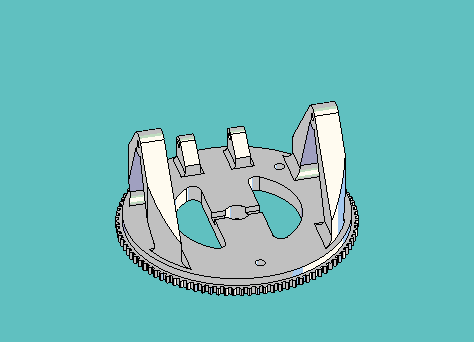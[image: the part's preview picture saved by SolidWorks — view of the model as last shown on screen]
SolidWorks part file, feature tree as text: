
SOLIDWORKS PART (.sldprt)
format: sldprt  version: not decoded by parser v0  size: 2,990,592 bytes
history: native  units: mm
features: sketch x17, cut_extrude x10, plane x7, extrude x6, fillet x3, material x1 (+11 scaffold rows collapsed)
feature tree (55):
  scaffold x11  (default folders/planes/origin — collapsed)
  material  "Material <not specified>"
  sketch  "Sketch1"  dims[c1.D1=50.8mm c1.D7=3.175mm c2.D1=88.9mm c2.D2=~93.32036mm c3.D2=45.0deg c3.D3=~94.913632mm c4.D3=45.0deg c4.D4=6.35mm c4.D5=6.35mm c4.D6=31.75mm]
  extrude  "Extrude1"  Depth=6.35mm
  sketch  "Sketch3"  dims[D1=3.4544mm D2=3.4544mm D3=9.525mm]
  cut_extrude  "Cut-Extrude2"  [1 undecoded]
  sketch  "Sketch5"  dims[c1.D3=19.05mm c1.D4=25.4mm c1.D1=20.6375mm c1.D2=20.6375mm c1.D5=~49.79749mm c2.D5=30.0deg c2.D6=11.1125mm c2.D1=17.145mm c2.D2=17.145mm c3.D1=~82.457251mm c4.D1=90.0deg c4.D2=9.525mm c4.D3=9.525mm]
  cut_extrude  "Cut-Extrude4"  [1 undecoded]
  sketch  "Sketch25"  dims[D1=4.7625mm]
  cut_extrude  "Cut-Extrude18"  [1 undecoded]
  fillet  "Fillet2"  Radius=3.175mm
  sketch  "Sketch6"  dims[D1=9.525mm]
  extrude  "Axis2"  [1 undecoded]
  plane  "Plane1"
  plane  "Plane2"
  plane  "Plane3"  Offset=50.8mm
  sketch  "Sketch11"  dims[c1.D1=40.3225mm c1.D2=40.3225mm c2.D1=22.86mm c2.D2=24.384mm c2.D3=30.1625mm c2.D4=30.1625mm]
  extrude  "Extrude6"  Depth=44.45mm
  sketch  "Sketch7"  dims[D1=2.7051mm D2=4.7625mm]
  cut_extrude  "Cut-Extrude7"  [1 undecoded]
  sketch  "Sketch12"  dims[D1=6.35mm D2=6.35mm D3=6.35mm]
  cut_extrude  "Cut-Extrude9"  [1 undecoded]
  sketch  "Sketch15"  dims[c1.D4=3.175mm c1.D1=9.525mm c1.D2=9.525mm c1.D3=9.525mm c2.D1=9.525mm c2.D2=9.525mm c2.D5=25.4mm c2.D6=25.4mm]
  cut_extrude  "Cut-Extrude12"  [1 undecoded]
  fillet  "Fillet3"  Radius=3.175mm
  plane  "Plane4"  Offset=7.14375mm
  plane  "Plane5"  Offset=7.14375mm
  sketch  "Sketch17"  dims[c1.D4=2.7051mm c1.D1=28.575mm c1.D2=9.525mm c1.D3=6.35mm c2.D1=38.1mm c2.D5=~9.745748mm c2.D3=9.525mm c3.D5=6.35mm c3.D6=3.175mm c3.D2=~11.90625mm c4.D5=~8.73125mm c4.D7=4.7625mm]
  extrude  "Extrude8"  Depth=5.969mm
  sketch  "Sketch18"  dims[D1=0.0mm]
  extrude  "Extrude9"  Depth=5.969mm
  fillet  "Fillet5"  Radius=1.5875mm
  plane  "Plane6"  Offset=39.6875mm
  plane  "Plane7"  Offset=39.6875mm
  sketch  "Sketch19"  dims[D1=12.7mm]
  cut_extrude  "Cut-Extrude14"  [1 undecoded]
  sketch  "Sketch20"
  cut_extrude  "Cut-Extrude15"  [1 undecoded]
  sketch  "Sketch21"  dims[D1=~2.38125mm]
  cut_extrude  "Cut-Extrude16"  [1 undecoded]
  sketch  "Sketch22"  dims[c1.D1=~90.71926mm c1.D4=~45.35963mm c2.D1=~45.35963mm c2.D4=~45.35963mm c2.D5=~45.35963mm c2.D9=2.0422mm c3.D1=45.3644mm c3.D2=~55.294757mm c4.D2=30.0deg c4.D3=~55.294757mm c5.D3=30.0deg c5.D4=~45.35963mm c5.D1=~2.999484mm c6.D4=~45.35963mm c6.D5=~45.35963mm c6.D2=0.809mm c6.D3=2.41mm c6.D6=1.19mm c6.D7=0.324mm c6.D8=0.1944mm c6.D9=0.1944mm c6.D10=1.19mm c7.D2=0.381mm c7.D3=1.2192mm c7.D4=2.413mm c7.D5=0.3302mm c7.D6=~49.397463mm c8.D6=1.8947deg c8.D7=~49.397463mm c9.D7=1.8947deg c9.D8=~0.11938mm c9.D9=~0.11938mm c9.D10=~0.19558mm c9.D11=~0.19558mm c9.D4=~282.002929mm c9.D1=~282.002929mm c10.D4=3.0mm c10.D5=1.5mm c10.D2=0.8128mm]
  extrude  "Extrude10"  Depth=3.175mm
  sketch  "Sketch24"  dims[c1.D1=~3.96875mm c1.D2=~3.96875mm c1.D3=~3.96875mm c1.D5=69.85mm c1.D4=~57.085134mm c2.D4=30.0deg c2.D6=~57.085134mm c3.D6=137.0deg c3.D7=~57.085134mm c4.D7=137.0deg]
  cut_extrude  "Cut-Extrude17"  [1 undecoded]
  sketch  "Sketch23"  dims[D1=93.218mm]
decode coverage: 24 of 36 modeling features carry decoded parameters
note: ~ marks probable driven/reference dimensions
note: 11 parameter values undecoded
summary: no parameter record found for 11 features
note: suppression state not decoded; provenance and decode notes live in map.json
